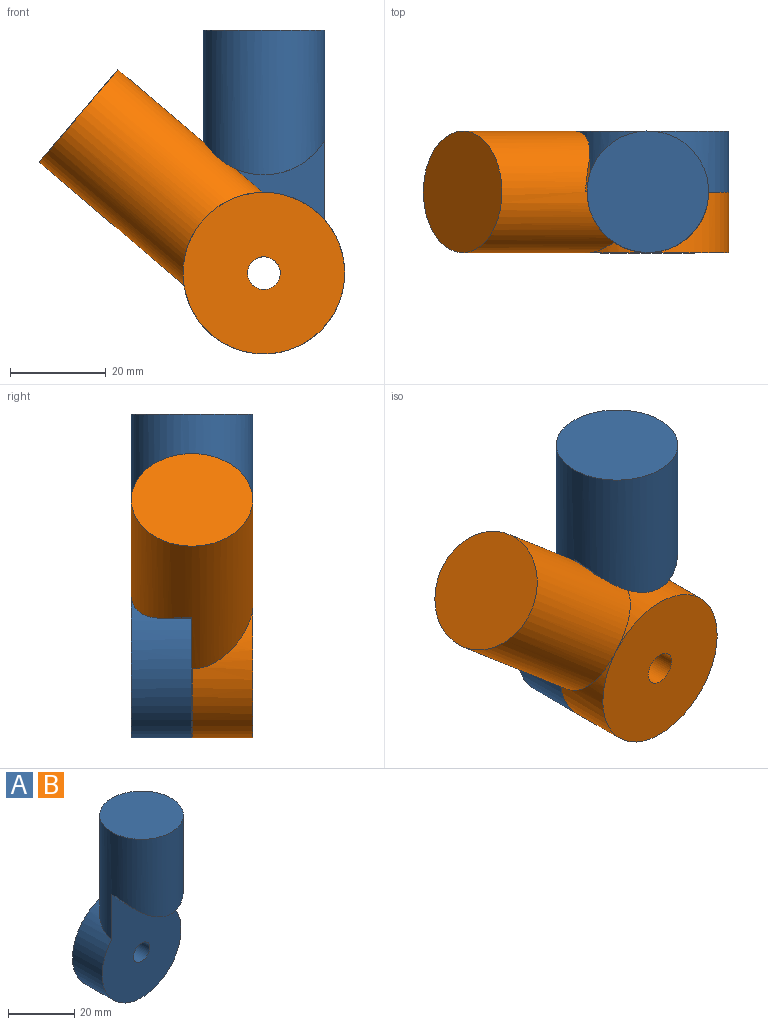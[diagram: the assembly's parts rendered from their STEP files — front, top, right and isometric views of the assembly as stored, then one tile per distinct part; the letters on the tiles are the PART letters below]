
ASSEMBLY  parts=2 mates=1
PART A: 7 faces, bbox 33.8x25.4x67.7 mm
  f0: cylinder r=12.7mm len=39.67mm, axis (0,0,-1), area 2535.2mm2, adj f1,f3,f4,f6
  f1: cylinder r=16.89mm len=33.78mm, axis (0,1,0), area 1071mm2, adj f0,f2,f4
  f2: plane 33.78x33.78mm, normal (0,1,0), area 859.3mm2, adj f1,f5
  f3: plane 25.4x25.4mm, normal (0,0,1), area 506.7mm2, adj f0
  f4: plane 44.72x33.78mm, normal (0,-1,0), area 1051.2mm2, adj f0,f1,f5,f6
  f5: cylinder r=3.43mm len=12.7mm, axis (0,-1,0), area 273.6mm2, adj f2,f4
  f6: cylinder r=14.72mm len=25.4mm, axis (0,-1,0), area 288.5mm2, adj f0,f4
PART B: same geometry as A
PLACE A t=(-4.28,4.25,13.29)mm fixed
PLACE B rot(axis=(0.42,0,-0.91),180deg) t=(-4.28,4.25,13.29)mm
MATE revolute B.f1 <-> A.f1  axis (0,1,0) through (-4.28,4.25,13.29)mm
